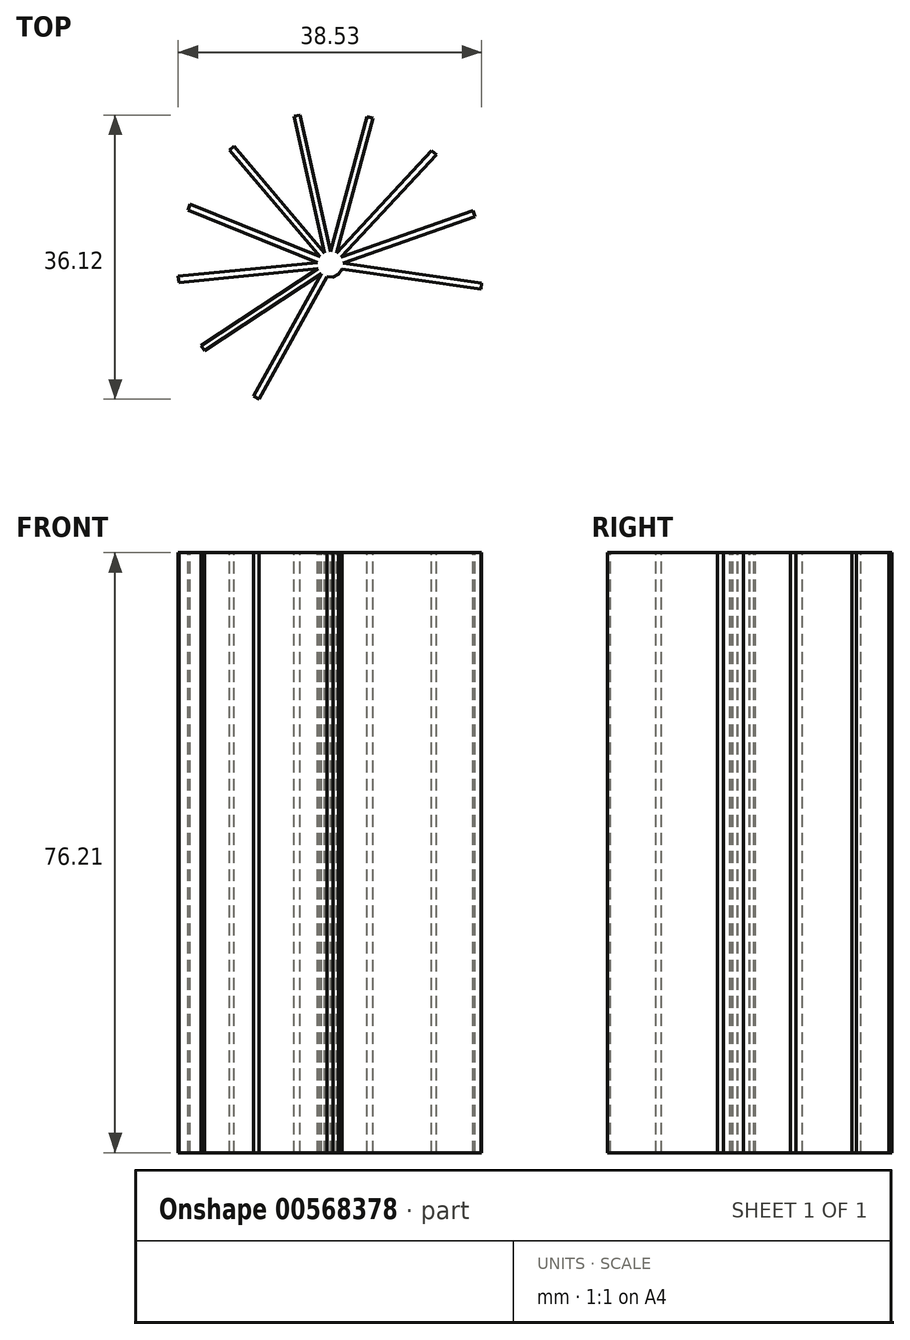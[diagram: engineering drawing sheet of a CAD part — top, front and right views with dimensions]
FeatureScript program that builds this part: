
annotation { "Feature Type Name" : "Feature", "Feature Type Description" : "" }
export const myFeature = defineFeature(function(context is Context, id is Id, definition is map)
    precondition{}
    {
        {
            var Q0;
            Q0=qCreatedBy(makeId("Top.planeOp"),FACE);
            var sketch = newSketch(context, id + "F0", { "sketchPlane" : qUnion([Q0])});
            skCircle(sketch, "E0", {"center": v(0, 0) * mm, "radius": 1.59 * mm});
            skSolve(sketch);
        }
        {
            var Q0;
            Q0=makeQuery(id+"F0.imprint","IMPRINT",FACE,{"disambiguationData":[TD([[makeQuery(id+"F0.imprint","IMPRINT",EDGE,{"derivedFrom":sQuery(id+"F0.wireOp",EDGE,"E0")}),1.0]])]});
            extrude(context, id + "F1", {"entities" : qUnion([Q0]), "endBound" : BoundingType.SYMMETRIC, "depth" : 76.2 * mm, "offsetDistance" : 25.4 * mm});
        }
        {
            var Q0;
            Q0=makeQuery(id+"F1.opExtrude","CAP_FACE",FACE,{"disambiguationData":[OSD([sQuery(id+"F0.wireOp",EDGE,"E0")])],"isStart":false});
            var sketch = newSketch(context, id + "F2", { "sketchPlane" : qUnion([Q0])});
            skCircle(sketch, "E1.cCircle", {"center": v(0, 0) * mm, "radius": 1.59 * mm, "construction": true});
            skLineSegment(sketch, "E1.0", {"start": v(-0.43, -1.58) * mm, "end": v(-1.11, -1.2) * mm});
            skLineSegment(sketch, "E1.1", {"start": v(-1.11, -1.2) * mm, "end": v(-1.54, -0.54) * mm});
            skLineSegment(sketch, "E1.2", {"start": v(-1.54, -0.54) * mm, "end": v(-1.62, 0.23) * mm});
            skLineSegment(sketch, "E1.3", {"start": v(-1.62, 0.23) * mm, "end": v(-1.32, 0.96) * mm});
            skLineSegment(sketch, "E1.4", {"start": v(-1.32, 0.96) * mm, "end": v(-0.73, 1.47) * mm});
            skLineSegment(sketch, "E1.5", {"start": v(-0.73, 1.47) * mm, "end": v(0.04, 1.64) * mm});
            skLineSegment(sketch, "E1.6", {"start": v(0.04, 1.64) * mm, "end": v(0.8, 1.43) * mm});
            skLineSegment(sketch, "E1.7", {"start": v(0.8, 1.43) * mm, "end": v(1.37, 0.9) * mm});
            skLineSegment(sketch, "E1.8", {"start": v(1.37, 0.9) * mm, "end": v(1.63, 0.16) * mm});
            skLineSegment(sketch, "E1.9", {"start": v(1.63, 0.16) * mm, "end": v(1.52, -0.61) * mm});
            skLineSegment(sketch, "E1.10", {"start": v(1.52, -0.61) * mm, "end": v(1.06, -1.25) * mm});
            skLineSegment(sketch, "E1.11", {"start": v(1.06, -1.25) * mm, "end": v(0.35, -1.6) * mm});
            skLineSegment(sketch, "E1.12", {"start": v(0.35, -1.6) * mm, "end": v(-0.43, -1.58) * mm});
            skPoint(sketch, "E1.0.midPoint", {"position": v(-0.77, -1.39) * mm});
            skSolve(sketch);
        }
        {
            var Q0;
            Q0 = qSketchRegion(id + "F2", true);
            extrude(context, id + "F3", {"entities" : qUnion([Q0]), "operationType" : NewBodyOperationType.ADD, "oppositeDirection" : true, "depth" : 76.2 * mm, "offsetDistance" : 25.4 * mm});
        }
        {
            var Q0;
            Q0=makeQuery(id+"F3.opExtrude","SWEPT_FACE",FACE,{"disambiguationData":[OSD([sQuery(id+"F2.wireOp",EDGE,"E1.0")])]});
            extrude(context, id + "F4", {"entities" : qUnion([Q0]), "operationType" : NewBodyOperationType.ADD, "depth" : 17.78 * mm, "offsetDistance" : 25.4 * mm});
        }
        {
            var Q0;
            Q0=makeQuery(id+"F3.opExtrude","SWEPT_FACE",FACE,{"disambiguationData":[OSD([sQuery(id+"F2.wireOp",EDGE,"E1.1")])]});
            extrude(context, id + "F5", {"entities" : qUnion([Q0]), "operationType" : NewBodyOperationType.ADD, "depth" : 17.78 * mm, "offsetDistance" : 25.4 * mm});
        }
        {
            var Q0;
            Q0=makeQuery(id+"F3.opExtrude","SWEPT_FACE",FACE,{"disambiguationData":[OSD([sQuery(id+"F2.wireOp",EDGE,"E1.2")])]});
            extrude(context, id + "F6", {"entities" : qUnion([Q0]), "operationType" : NewBodyOperationType.ADD, "depth" : 17.78 * mm, "offsetDistance" : 25.4 * mm});
        }
        {
            var Q0;
            Q0=makeQuery(id+"F3.opExtrude","SWEPT_FACE",FACE,{"disambiguationData":[OSD([sQuery(id+"F2.wireOp",EDGE,"E1.3")])]});
            extrude(context, id + "F7", {"entities" : qUnion([Q0]), "operationType" : NewBodyOperationType.ADD, "depth" : 17.78 * mm, "offsetDistance" : 25.4 * mm});
        }
        {
            var Q0;
            Q0=makeQuery(id+"F3.opExtrude","SWEPT_FACE",FACE,{"disambiguationData":[OSD([sQuery(id+"F2.wireOp",EDGE,"E1.4")])]});
            extrude(context, id + "F8", {"entities" : qUnion([Q0]), "operationType" : NewBodyOperationType.ADD, "depth" : 17.78 * mm, "offsetDistance" : 25.4 * mm});
        }
        {
            var Q0;
            Q0=makeQuery(id+"F3.opExtrude","SWEPT_FACE",FACE,{"disambiguationData":[OSD([sQuery(id+"F2.wireOp",EDGE,"E1.5")])]});
            extrude(context, id + "F9", {"entities" : qUnion([Q0]), "operationType" : NewBodyOperationType.ADD, "depth" : 17.78 * mm, "offsetDistance" : 25.4 * mm});
        }
        {
            var Q0;
            Q0=makeQuery(id+"F3.opExtrude","SWEPT_FACE",FACE,{"disambiguationData":[OSD([sQuery(id+"F2.wireOp",EDGE,"E1.6")])]});
            extrude(context, id + "F10", {"entities" : qUnion([Q0]), "operationType" : NewBodyOperationType.ADD, "depth" : 17.78 * mm, "offsetDistance" : 25.4 * mm});
        }
        {
            var Q0;
            Q0=makeQuery(id+"F3.opExtrude","SWEPT_FACE",FACE,{"disambiguationData":[OSD([sQuery(id+"F2.wireOp",EDGE,"E1.7")])]});
            extrude(context, id + "F11", {"entities" : qUnion([Q0]), "operationType" : NewBodyOperationType.ADD, "depth" : 17.78 * mm, "offsetDistance" : 25.4 * mm});
        }
        {
            var Q0;
            Q0=makeQuery(id+"F3.opExtrude","SWEPT_FACE",FACE,{"disambiguationData":[OSD([sQuery(id+"F2.wireOp",EDGE,"E1.8")])]});
            extrude(context, id + "F12", {"entities" : qUnion([Q0]), "operationType" : NewBodyOperationType.ADD, "depth" : 17.78 * mm, "offsetDistance" : 25.4 * mm});
        }
        {
            var Q0;
            Q0=makeQuery(id+"F3.opExtrude","SWEPT_FACE",FACE,{"disambiguationData":[OSD([sQuery(id+"F2.wireOp",EDGE,"E1.9")])]});
            extrude(context, id + "F13", {"entities" : qUnion([Q0]), "operationType" : NewBodyOperationType.ADD, "depth" : 17.78 * mm, "offsetDistance" : 25.4 * mm});
        }
    });
